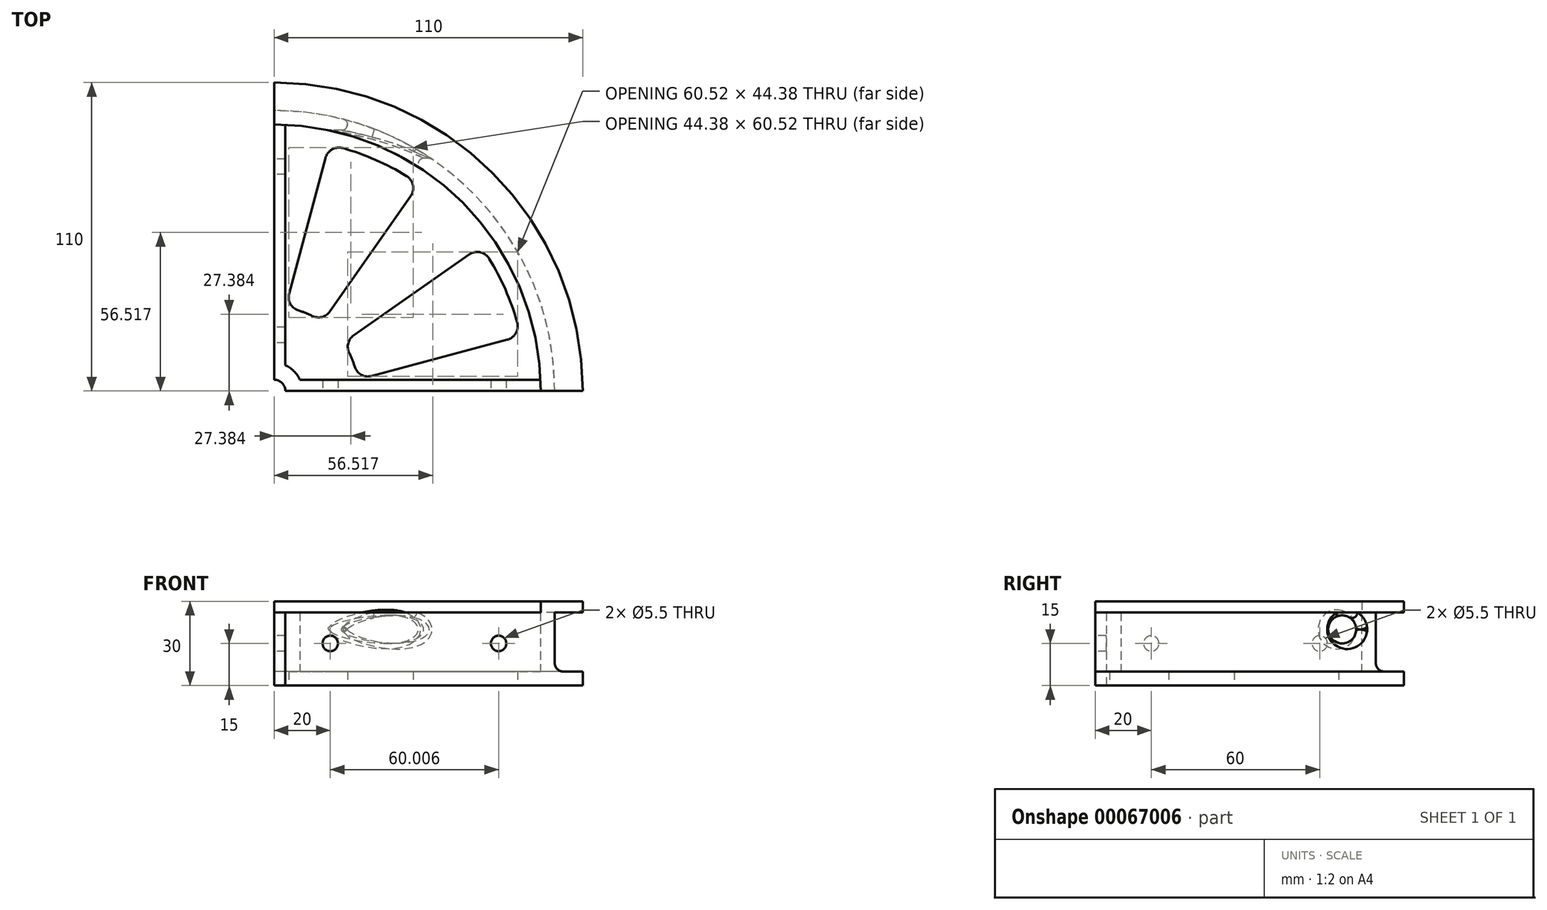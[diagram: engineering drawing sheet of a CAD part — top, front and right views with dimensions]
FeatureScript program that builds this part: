
annotation { "Feature Type Name" : "Feature", "Feature Type Description" : "" }
export const myFeature = defineFeature(function(context is Context, id is Id, definition is map)
    precondition{}
    {
        {
            var Q0;
            Q0=qCreatedBy(makeId("Top.planeOp"),FACE);
            var sketch = newSketch(context, id + "F0", { "sketchPlane" : qUnion([Q0])});
            skArc(sketch, "E0", {"start": v(110, 0) * mm, "mid": v(77.78, 77.78) * mm, "end": v(0, 110) * mm});
            skArc(sketch, "E1", {"start": v(4, 0) * mm, "mid": v(2.83, 2.83) * mm, "end": v(0, 4) * mm});
            skLineSegment(sketch, "E2", {"start": v(0, 110) * mm, "end": v(0, 4) * mm});
            skLineSegment(sketch, "E3", {"start": v(4, 0) * mm, "end": v(110, 0) * mm});
            skArc(sketch, "E4", {"start": v(8.73, 28.7) * mm, "mid": v(11.17, 27.84) * mm, "end": v(13.52, 26.78) * mm});
            skArc(sketch, "E5", {"start": v(26.78, 13.52) * mm, "mid": v(27.84, 11.17) * mm, "end": v(28.7, 8.73) * mm});
            skArc(sketch, "E6", {"start": v(24.49, 86.6) * mm, "mid": v(36.19, 82.4) * mm, "end": v(47.2, 76.63) * mm});
            skArc(sketch, "E7", {"start": v(76.63, 47.2) * mm, "mid": v(82.4, 36.19) * mm, "end": v(86.6, 24.49) * mm});
            skLineSegment(sketch, "E8", {"start": v(5.35, 34.78) * mm, "end": v(18.3, 83.09) * mm});
            skLineSegment(sketch, "E9", {"start": v(19.87, 28.38) * mm, "end": v(48.67, 69.5) * mm});
            skLineSegment(sketch, "E10", {"start": v(28.38, 19.87) * mm, "end": v(69.5, 48.67) * mm});
            skLineSegment(sketch, "E11", {"start": v(34.78, 5.35) * mm, "end": v(83.09, 18.3) * mm});
            skPoint(sketch, "E12.visualSharp", {"position": v(19.57, 87.85) * mm});
            skArc(sketch, "E12.filletArc", {"start": v(24.49, 86.6) * mm, "mid": v(20.66, 86.14) * mm, "end": v(18.3, 83.09) * mm});
            skPoint(sketch, "E13.visualSharp", {"position": v(51.62, 73.72) * mm});
            skArc(sketch, "E13.filletArc", {"start": v(48.67, 69.5) * mm, "mid": v(49.47, 73.39) * mm, "end": v(47.2, 76.63) * mm});
            skPoint(sketch, "E14.visualSharp", {"position": v(4, 29.73) * mm});
            skArc(sketch, "E14.filletArc", {"start": v(5.35, 34.78) * mm, "mid": v(5.81, 31.06) * mm, "end": v(8.73, 28.7) * mm});
            skPoint(sketch, "E15.visualSharp", {"position": v(17.2, 24.57) * mm});
            skArc(sketch, "E15.filletArc", {"start": v(13.52, 26.78) * mm, "mid": v(17, 26.4) * mm, "end": v(19.87, 28.38) * mm});
            skPoint(sketch, "E16.visualSharp", {"position": v(24.57, 17.2) * mm});
            skArc(sketch, "E16.filletArc", {"start": v(28.38, 19.87) * mm, "mid": v(26.4, 17) * mm, "end": v(26.78, 13.52) * mm});
            skPoint(sketch, "E17.visualSharp", {"position": v(29.73, 4) * mm});
            skArc(sketch, "E17.filletArc", {"start": v(28.7, 8.73) * mm, "mid": v(31.06, 5.81) * mm, "end": v(34.78, 5.35) * mm});
            skPoint(sketch, "E18.visualSharp", {"position": v(87.85, 19.57) * mm});
            skArc(sketch, "E18.filletArc", {"start": v(83.09, 18.3) * mm, "mid": v(86.14, 20.66) * mm, "end": v(86.6, 24.49) * mm});
            skPoint(sketch, "E19.visualSharp", {"position": v(73.72, 51.62) * mm});
            skArc(sketch, "E19.filletArc", {"start": v(76.63, 47.2) * mm, "mid": v(73.39, 49.47) * mm, "end": v(69.5, 48.67) * mm});
            skSolve(sketch);
        }
        {
            var Q0;
            Q0 = qSketchRegion(id + "F0", true);
            extrude(context, id + "F1", {"entities" : qUnion([Q0]), "depth" : 5 * mm});
        }
        {
            var Q0;
            Q0=makeQuery(id+"F1.opExtrude","CAP_FACE",FACE,{"disambiguationData":[OSD([sQuery(id+"F0.wireOp",EDGE,"E0"),sQuery(id+"F0.wireOp",EDGE,"E1"),sQuery(id+"F0.wireOp",EDGE,"E2"),sQuery(id+"F0.wireOp",EDGE,"E3"),sQuery(id+"F0.wireOp",EDGE,"E4"),sQuery(id+"F0.wireOp",EDGE,"E5"),sQuery(id+"F0.wireOp",EDGE,"E6"),sQuery(id+"F0.wireOp",EDGE,"E7"),sQuery(id+"F0.wireOp",EDGE,"E8"),sQuery(id+"F0.wireOp",EDGE,"E9"),sQuery(id+"F0.wireOp",EDGE,"E10"),sQuery(id+"F0.wireOp",EDGE,"E11"),sQuery(id+"F0.wireOp",EDGE,"E12.filletArc"),sQuery(id+"F0.wireOp",EDGE,"E13.filletArc"),sQuery(id+"F0.wireOp",EDGE,"E14.filletArc"),sQuery(id+"F0.wireOp",EDGE,"E15.filletArc"),sQuery(id+"F0.wireOp",EDGE,"E16.filletArc"),sQuery(id+"F0.wireOp",EDGE,"E17.filletArc"),sQuery(id+"F0.wireOp",EDGE,"E18.filletArc"),sQuery(id+"F0.wireOp",EDGE,"E19.filletArc")])],"isStart":false});
            var sketch = newSketch(context, id + "F2", { "sketchPlane" : qUnion([Q0])});
            skArc(sketch, "E20", {"start": v(0, 4) * mm, "mid": v(2.83, 2.83) * mm, "end": v(4, 0) * mm});
            skArc(sketch, "E21", {"start": v(0, 10) * mm, "mid": v(7.07, 7.07) * mm, "end": v(10, 0) * mm});
            skLineSegment(sketch, "E22", {"start": v(0, 4) * mm, "end": v(0, 10) * mm});
            skLineSegment(sketch, "E23", {"start": v(4, 0) * mm, "end": v(10, 0) * mm});
            skArc(sketch, "E24", {"start": v(95, 0) * mm, "mid": v(67.18, 67.18) * mm, "end": v(0, 95) * mm});
            skArc(sketch, "E25", {"start": v(100, 0) * mm, "mid": v(70.71, 70.71) * mm, "end": v(0, 100) * mm});
            skLineSegment(sketch, "E26", {"start": v(0, 95) * mm, "end": v(0, 100) * mm});
            skLineSegment(sketch, "E27", {"start": v(95, 0) * mm, "end": v(100, 0) * mm});
            skSolve(sketch);
        }
        {
            var Q0;
            Q0 = qSketchRegion(id + "F2", true);
            extrude(context, id + "F3", {"entities" : qUnion([Q0]), "operationType" : NewBodyOperationType.ADD, "depth" : 21 * mm});
        }
        {
            var Q0;
            Q0=makeQuery(id+"F3.opExtrude","CAP_FACE",FACE,{"disambiguationData":[OSD([sQuery(id+"F2.wireOp",EDGE,"E24"),sQuery(id+"F2.wireOp",EDGE,"E25"),sQuery(id+"F2.wireOp",EDGE,"E26"),sQuery(id+"F2.wireOp",EDGE,"E27")])],"isStart":false});
            var sketch = newSketch(context, id + "F4", { "sketchPlane" : qUnion([Q0])});
            skArc(sketch, "E28", {"start": v(95, 0) * mm, "mid": v(67.18, 67.18) * mm, "end": v(0, 95) * mm});
            skArc(sketch, "E29", {"start": v(110, 0) * mm, "mid": v(77.78, 77.78) * mm, "end": v(0, 110) * mm});
            skLineSegment(sketch, "E30", {"start": v(0, 95) * mm, "end": v(0, 110) * mm});
            skLineSegment(sketch, "E31", {"start": v(95, 0) * mm, "end": v(110, 0) * mm});
            skSolve(sketch);
        }
        {
            var Q0;
            Q0 = qSketchRegion(id + "F4", true);
            extrude(context, id + "F5", {"entities" : qUnion([Q0]), "operationType" : NewBodyOperationType.ADD, "depth" : 4 * mm});
        }
        {
            var Q0;
            Q0=makeQuery(id+"F5.boolean.opBoolean","MERGE",FACE,{"derivedFrom":[makeQuery(id+"F3.boolean.opBoolean","MERGE",FACE,{"derivedFrom":[makeQuery(id+"F1.opExtrude","SWEPT_FACE",FACE,{"disambiguationData":[OSD([sQuery(id+"F0.wireOp",EDGE,"E3")])]}),makeQuery(id+"F3.opExtrude","SWEPT_FACE",FACE,{"disambiguationData":[OSD([sQuery(id+"F2.wireOp",EDGE,"E23")])]}),makeQuery(id+"F3.opExtrude","SWEPT_FACE",FACE,{"disambiguationData":[OSD([sQuery(id+"F2.wireOp",EDGE,"E27")])]})]}),makeQuery(id+"F5.opExtrude","SWEPT_FACE",FACE,{"disambiguationData":[OSD([sQuery(id+"F4.wireOp",EDGE,"E31")])]})]});
            var sketch = newSketch(context, id + "F6", { "sketchPlane" : qUnion([Q0])});
            skLineSegment(sketch, "E32.bottom", {"start": v(4, 4.23) * mm, "end": v(95, 4.23) * mm});
            skLineSegment(sketch, "E32.top", {"start": v(4, 26) * mm, "end": v(95, 26) * mm});
            skLineSegment(sketch, "E32.right", {"start": v(95, 4.23) * mm, "end": v(95, 26) * mm});
            skCircle(sketch, "E33", {"center": v(20, 15) * mm, "radius": 2.75 * mm});
            skCircle(sketch, "E34", {"center": v(80, 15) * mm, "radius": 2.75 * mm});
            skLineSegment(sketch, "E35", {"start": v(4, 26) * mm, "end": v(4, 4.23) * mm});
            skSolve(sketch);
        }
        {
            var Q0;
            Q0 = qSketchRegion(id + "F6", true);
            extrude(context, id + "F7", {"entities" : qUnion([Q0]), "operationType" : NewBodyOperationType.ADD, "oppositeDirection" : true, "depth" : 4 * mm});
        }
        {
            var Q0;
            Q0=makeQuery(id+"F5.boolean.opBoolean","MERGE",FACE,{"derivedFrom":[makeQuery(id+"F3.boolean.opBoolean","MERGE",FACE,{"derivedFrom":[makeQuery(id+"F1.opExtrude","SWEPT_FACE",FACE,{"disambiguationData":[OSD([sQuery(id+"F0.wireOp",EDGE,"E2")])]}),makeQuery(id+"F3.opExtrude","SWEPT_FACE",FACE,{"disambiguationData":[OSD([sQuery(id+"F2.wireOp",EDGE,"E22")])]}),makeQuery(id+"F3.opExtrude","SWEPT_FACE",FACE,{"disambiguationData":[OSD([sQuery(id+"F2.wireOp",EDGE,"E26")])]})]}),makeQuery(id+"F5.opExtrude","SWEPT_FACE",FACE,{"disambiguationData":[OSD([sQuery(id+"F4.wireOp",EDGE,"E30")])]})]});
            var sketch = newSketch(context, id + "F8", { "sketchPlane" : qUnion([Q0])});
            skCircle(sketch, "E36", {"center": v(-88, 20) * mm, "radius": 5 * mm});
            skSolve(sketch);
        }
        {
            var Q0;
            Q0 = qSketchRegion(id + "F8", true);
            extrude(context, id + "F9", {"entities" : qUnion([Q0]), "operationType" : NewBodyOperationType.REMOVE, "endBound" : BoundingType.THROUGH_ALL, "oppositeDirection" : true, "depth" : 25 * mm});
        }
        {
            var Q0;
            Q0=makeQuery(id+"F5.boolean.opBoolean","MERGE",FACE,{"derivedFrom":[makeQuery(id+"F3.boolean.opBoolean","MERGE",FACE,{"derivedFrom":[makeQuery(id+"F1.opExtrude","SWEPT_FACE",FACE,{"disambiguationData":[OSD([sQuery(id+"F0.wireOp",EDGE,"E2")])]}),makeQuery(id+"F3.opExtrude","SWEPT_FACE",FACE,{"disambiguationData":[OSD([sQuery(id+"F2.wireOp",EDGE,"E22")])]}),makeQuery(id+"F3.opExtrude","SWEPT_FACE",FACE,{"disambiguationData":[OSD([sQuery(id+"F2.wireOp",EDGE,"E26")])]})]}),makeQuery(id+"F5.opExtrude","SWEPT_FACE",FACE,{"disambiguationData":[OSD([sQuery(id+"F4.wireOp",EDGE,"E30")])]})]});
            var sketch = newSketch(context, id + "F10", { "sketchPlane" : qUnion([Q0])});
            skLineSegment(sketch, "E37.bottom", {"start": v(-4, 26) * mm, "end": v(-95, 26) * mm});
            skLineSegment(sketch, "E37.top", {"start": v(-4, 5) * mm, "end": v(-95, 5) * mm});
            skLineSegment(sketch, "E37.left", {"start": v(-4, 26) * mm, "end": v(-4, 5) * mm});
            skLineSegment(sketch, "E37.right", {"start": v(-95, 26) * mm, "end": v(-95, 5) * mm});
            skCircle(sketch, "E38", {"center": v(-80, 15) * mm, "radius": 2.75 * mm});
            skCircle(sketch, "E39", {"center": v(-20, 15) * mm, "radius": 2.75 * mm});
            skSolve(sketch);
        }
        {
            var Q0;
            Q0 = qSketchRegion(id + "F10", true);
            extrude(context, id + "F11", {"entities" : qUnion([Q0]), "operationType" : NewBodyOperationType.ADD, "oppositeDirection" : true, "depth" : 4 * mm});
        }
        {
            var Q0;
            Q0=makeQuery(id+"F3.opExtrude","CAP_EDGE",EDGE,{"disambiguationData":[OSD([sQuery(id+"F2.wireOp",EDGE,"E25")])],"isStart":false});
            var Q1;
            Q1=makeQuery(id+"F3.opExtrude","CAP_EDGE",EDGE,{"disambiguationData":[OSD([sQuery(id+"F2.wireOp",EDGE,"E25")])],"isStart":true});
            fillet(context, id + "F12", {"entities" : qUnion([Q0, Q1]), "radius" : 3 * mm, "tangentPropagation" : true, "allowEdgeOverflow" : false});
        }
        {
            var Q0;
            Q0=makeQuery(id+"F9.boolean.opBoolean","INTERSECT",EDGE,{"derivedFrom":[makeQuery(id+"F5.boolean.opBoolean","MERGE",FACE,{"derivedFrom":[makeQuery(id+"F3.opExtrude","SWEPT_FACE",FACE,{"disambiguationData":[OSD([sQuery(id+"F2.wireOp",EDGE,"E24")])]}),makeQuery(id+"F5.opExtrude","SWEPT_FACE",FACE,{"disambiguationData":[OSD([sQuery(id+"F4.wireOp",EDGE,"E28")])]})]}),makeQuery(id+"F9.opExtrude","SWEPT_FACE",FACE,{"disambiguationData":[OSD([sQuery(id+"F8.wireOp",EDGE,"E36")])]})]});
            var Q1;
            Q1=makeQuery(id+"F9.boolean.opBoolean","INTERSECT",EDGE,{"derivedFrom":[makeQuery(id+"F3.opExtrude","SWEPT_FACE",FACE,{"disambiguationData":[OSD([sQuery(id+"F2.wireOp",EDGE,"E25")])]}),makeQuery(id+"F9.opExtrude","SWEPT_FACE",FACE,{"disambiguationData":[OSD([sQuery(id+"F8.wireOp",EDGE,"E36")])]})]});
            fillet(context, id + "F13", {"entities" : qUnion([Q0, Q1]), "radius" : 2 * mm, "tangentPropagation" : true, "allowEdgeOverflow" : false});
        }
    });
